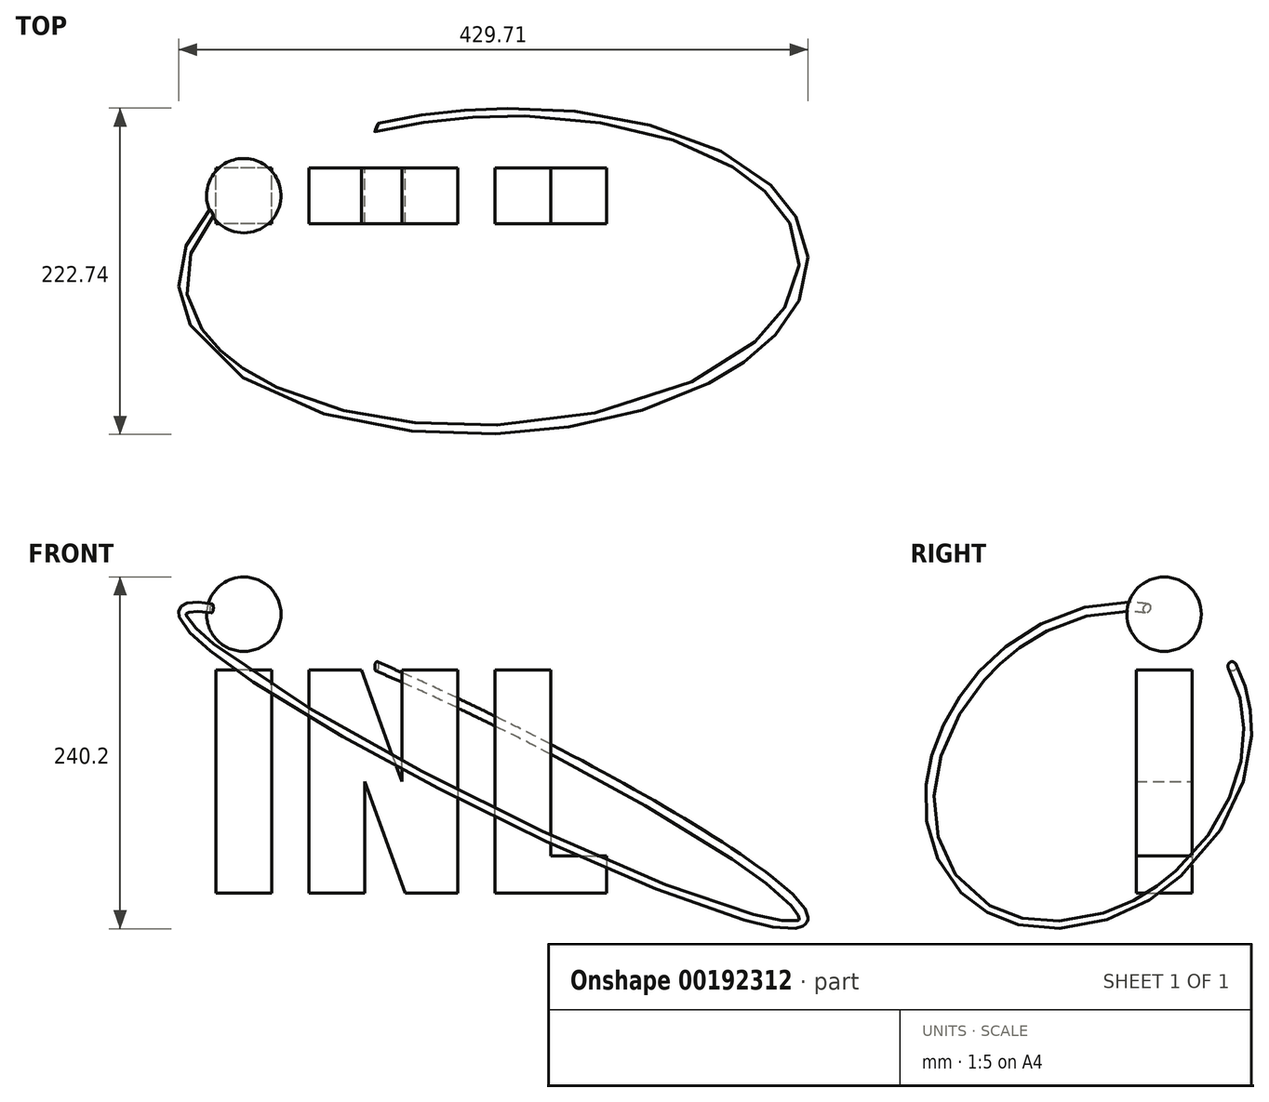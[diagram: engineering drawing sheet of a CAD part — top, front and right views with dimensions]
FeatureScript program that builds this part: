
annotation { "Feature Type Name" : "Feature", "Feature Type Description" : "" }
export const myFeature = defineFeature(function(context is Context, id is Id, definition is map)
    precondition{}
    {
        {
            var Q0;
            Q0=qCreatedBy(makeId("Front.planeOp"),FACE);
            var sketch = newSketch(context, id + "F0", { "sketchPlane" : qUnion([Q0])});
            skLineSegment(sketch, "E0.bottom", {"start": v(-101.6, 0) * mm, "end": v(-139.7, 0) * mm});
            skLineSegment(sketch, "E0.top", {"start": v(-101.6, 152.4) * mm, "end": v(-139.7, 152.4) * mm});
            skLineSegment(sketch, "E0.left", {"start": v(-101.6, 0) * mm, "end": v(-101.6, 152.4) * mm});
            skLineSegment(sketch, "E0.right", {"start": v(-139.7, 0) * mm, "end": v(-139.7, 152.4) * mm});
            skLineSegment(sketch, "E1", {"start": v(-76.2, 0) * mm, "end": v(-76.2, 152.4) * mm});
            skLineSegment(sketch, "E2", {"start": v(-76.2, 152.4) * mm, "end": v(-40.43, 152.4) * mm});
            skLineSegment(sketch, "E3", {"start": v(-40.43, 152.4) * mm, "end": v(-12.7, 76.2) * mm});
            skLineSegment(sketch, "E4", {"start": v(-12.7, 76.2) * mm, "end": v(-12.7, 152.4) * mm});
            skLineSegment(sketch, "E5", {"start": v(-12.7, 152.4) * mm, "end": v(25.4, 152.4) * mm});
            skLineSegment(sketch, "E6", {"start": v(25.4, 152.4) * mm, "end": v(25.4, 0) * mm});
            skLineSegment(sketch, "E7", {"start": v(25.4, 0) * mm, "end": v(-10.37, 0) * mm});
            skLineSegment(sketch, "E8", {"start": v(-10.37, 0) * mm, "end": v(-38.1, 76.2) * mm});
            skLineSegment(sketch, "E9", {"start": v(-38.1, 76.2) * mm, "end": v(-38.1, 0) * mm});
            skLineSegment(sketch, "E10", {"start": v(-38.1, 0) * mm, "end": v(-76.2, 0) * mm});
            skLineSegment(sketch, "E11", {"start": v(50.8, 0) * mm, "end": v(50.8, 152.4) * mm});
            skLineSegment(sketch, "E12", {"start": v(50.8, 152.4) * mm, "end": v(88.9, 152.4) * mm});
            skLineSegment(sketch, "E13", {"start": v(88.9, 152.4) * mm, "end": v(88.9, 25.4) * mm});
            skLineSegment(sketch, "E14", {"start": v(88.9, 25.4) * mm, "end": v(127, 25.4) * mm});
            skLineSegment(sketch, "E15", {"start": v(127, 25.4) * mm, "end": v(127, 0) * mm});
            skLineSegment(sketch, "E16", {"start": v(127, 0) * mm, "end": v(50.8, 0) * mm});
            skSolve(sketch);
        }
        {
            var Q0;
            Q0 = qSketchRegion(id + "F0", true);
            extrude(context, id + "F1", {"entities" : qUnion([Q0]), "depth" : 38.1 * mm});
        }
        {
            var Q0;
            Q0=qCreatedBy(makeId("Front.planeOp"),FACE);
            cPlane(context, id + "F2", {"entities" : qUnion([Q0]), "cplaneType" : CPlaneType.OFFSET, "offset" : 19.05 * mm, "width" : 152.4 * mm, "height" : 152.4 * mm});
        }
        {
            var Q0;
            Q0=qCreatedBy(id+"F2.planeOp",FACE);
            var sketch = newSketch(context, id + "F3", { "sketchPlane" : qUnion([Q0])});
            skLineSegment(sketch, "E17", {"start": v(-120.65, 0) * mm, "end": v(-120.65, 210.33) * mm, "construction": true});
            skArc(sketch, "E18", {"start": v(-120.65, 165.1) * mm, "mid": v(-95.25, 190.5) * mm, "end": v(-120.65, 215.9) * mm});
            skLineSegment(sketch, "E19", {"start": v(-120.65, 215.9) * mm, "end": v(-120.65, 165.1) * mm});
            skSolve(sketch);
        }
        {
            var Q0;
            Q0 = qSketchRegion(id + "F3", true);
            var Q1;
            Q1=sQuery(id+"F3.wireOp",EDGE,"E17");
            revolve(context, id + "F4", {"entities" : qUnion([Q0]), "axis" : qUnion([Q1]), "revolveType" : RevolveType.FULL});
        }
        {
            var Q0;
            Q0=qCreatedBy(makeId("Top.planeOp"),FACE);
            var sketch = newSketch(context, id + "F5", { "sketchPlane" : qUnion([Q0])});
            skLineSegment(sketch, "E20", {"start": v(0, 0) * mm, "end": v(-91.77, -158.94) * mm, "construction": true});
            skLineSegment(sketch, "E21", {"start": v(-91.77, -158.94) * mm, "end": v(84.52, 146.4) * mm, "construction": true});
            skLineSegment(sketch, "E22", {"start": v(0, 113.6) * mm, "end": v(0, -137.01) * mm, "construction": true});
            skSolve(sketch);
        }
        {
            var Q0;
            Q0=qCreatedBy(makeId("Top.planeOp"),FACE);
            var Q1;
            Q1=sQuery(id+"F5.wireOp",EDGE,"E21");
            cPlane(context, id + "F6", {"entities" : qUnion([Q0, Q1]), "cplaneType" : CPlaneType.LINE_ANGLE, "offset" : 25.4 * mm, "angle" : 30 * degree, "width" : 152.4 * mm, "height" : 152.4 * mm});
        }
        {
            var Q0;
            Q0=qCreatedBy(id+"F6.planeOp",FACE);
            cPlane(context, id + "F7", {"entities" : qUnion([Q0]), "cplaneType" : CPlaneType.OFFSET, "offset" : 114.3 * mm, "oppositeDirection" : true, "width" : 152.4 * mm, "height" : 152.4 * mm});
        }
        {
            var Q0;
            Q0=qCreatedBy(id+"F7.planeOp",FACE);
            var sketch = newSketch(context, id + "F8", { "sketchPlane" : qUnion([Q0])});
            skEllipticalArc(sketch, "E23", {});
            skLineSegment(sketch, "E24", {"start": v(0, 43.67) * mm, "end": v(-88.2, -69.21) * mm, "construction": true});
            skLineSegment(sketch, "E25", {"start": v(0, 43.67) * mm, "end": v(-194.99, -37.89) * mm, "construction": true});
            const initialGuessF8  = {"E23": [0, 0.043669410049915314, -0.9925359175666486, -0.12195266434207541, 0.23656061852467103, 0.11207979426850406, 1.128225884111132, 0.5352469164286614]};
            skSetInitialGuess(sketch, initialGuessF8);
            skSolve(sketch);
        }
        {
            var Q0;
            Q0=makeQuery(id+"F1.opExtrude","SWEPT_FACE",FACE,{"disambiguationData":[OSD([sQuery(id+"F0.wireOp",EDGE,"E0.right")])]});
            var Q1;
            Q1=sQuery(id+"F8.wireOp",VERTEX,"E23.end");
            cPlane(context, id + "F9", {"entities" : qUnion([Q0, Q1]), "cplaneType" : CPlaneType.PLANE_POINT, "offset" : 25.4 * mm, "oppositeDirection" : true, "width" : 152.4 * mm, "height" : 152.4 * mm});
        }
        {
            var Q0;
            Q0=qCreatedBy(id+"F9.planeOp",FACE);
            var sketch = newSketch(context, id + "F10", { "sketchPlane" : qUnion([Q0])});
            skCircle(sketch, "E26", {"center": v(15.54, 190.64) * mm, "radius": 3.18 * mm});
            skSolve(sketch);
        }
        {
            var Q0;
            Q0 = qSketchRegion(id + "F10", true);
            var Q1;
            Q1=sQuery(id+"F10.wireOp",EDGE,"E26");
            var Q2;
            Q2=sQuery(id+"F8.wireOp",EDGE,"E23");
            sweep(context, id + "F11", {"operationType" : NewBodyOperationType.ADD, "profiles" : qUnion([Q0]), "surfaceProfiles" : qUnion([Q1]), "path" : qUnion([Q2])});
        }
    });
